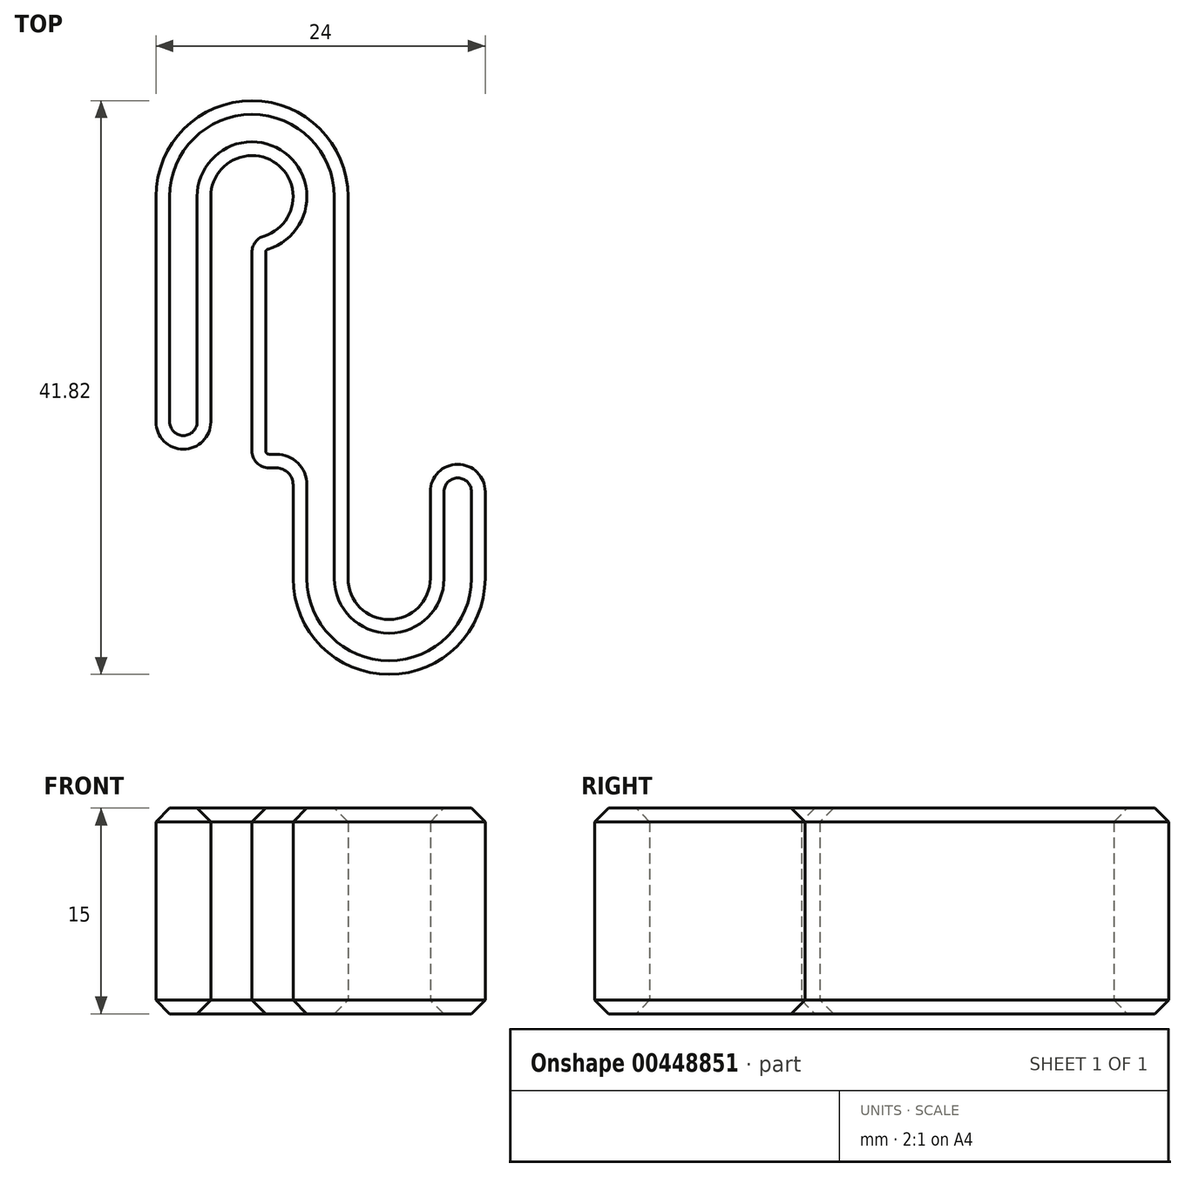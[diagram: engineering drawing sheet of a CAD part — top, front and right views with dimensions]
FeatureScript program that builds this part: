
annotation { "Feature Type Name" : "Feature", "Feature Type Description" : "" }
export const myFeature = defineFeature(function(context is Context, id is Id, definition is map)
    precondition{}
    {
        {
            var Q0;
            Q0=qCreatedBy(makeId("Top.planeOp"),FACE);
            var sketch = newSketch(context, id + "F0", { "sketchPlane" : qUnion([Q0])});
            skLineSegment(sketch, "E0.left", {"start": v(-10, 8.42) * mm, "end": v(-10, -8) * mm});
            skLineSegment(sketch, "E0.right", {"start": v(0, 8.42) * mm, "end": v(0, -19.4) * mm});
            skLineSegment(sketch, "E1.left", {"start": v(10, 13.42) * mm, "end": v(10, -13.09) * mm});
            skArc(sketch, "E2", {"start": v(0, 8.42) * mm, "mid": v(-5, 13.42) * mm, "end": v(-10, 8.42) * mm});
            skArc(sketch, "E3", {"start": v(0, -19.4) * mm, "mid": v(5, -24.4) * mm, "end": v(10, -19.4) * mm});
            skPoint(sketch, "E4.orphan", {"position": v(0, -24.4) * mm});
            skLineSegment(sketch, "E5", {"start": v(10, -13.09) * mm, "end": v(10, -19.4) * mm});
            skLineSegment(sketch, "E6", {"start": v(-10, -8) * mm, "end": v(-10, -24.4) * mm});
            skArc(sketch, "E7.0.startCap", {"start": v(-12, 8.42) * mm, "mid": v(-10, 10.42) * mm, "end": v(-8, 8.42) * mm});
            skArc(sketch, "E7.0.endCap", {"start": v(-8, -8) * mm, "mid": v(-10, -10) * mm, "end": v(-12, -8) * mm});
            skLineSegment(sketch, "E7.0.left", {"start": v(-8, 8.42) * mm, "end": v(-8, -8) * mm});
            skLineSegment(sketch, "E7.0.right", {"start": v(-12, 8.42) * mm, "end": v(-12, -8) * mm});
            skArc(sketch, "E7.1.startCap", {"start": v(2, 8.42) * mm, "mid": v(0, 6.42) * mm, "end": v(-2, 8.42) * mm});
            skArc(sketch, "E7.1.endCap", {"start": v(-8, 8.42) * mm, "mid": v(-10, 6.42) * mm, "end": v(-12, 8.42) * mm});
            skArc(sketch, "E7.1.left", {"start": v(-2, 8.42) * mm, "mid": v(-5, 11.42) * mm, "end": v(-8, 8.42) * mm});
            skArc(sketch, "E7.1.right", {"start": v(2, 8.42) * mm, "mid": v(-5, 15.42) * mm, "end": v(-12, 8.42) * mm});
            skArc(sketch, "E7.2.startCap", {"start": v(-2, 8.42) * mm, "mid": v(0, 10.42) * mm, "end": v(2, 8.42) * mm});
            skArc(sketch, "E7.2.endCap", {"start": v(2, -19.4) * mm, "mid": v(0, -21.4) * mm, "end": v(-2, -19.4) * mm});
            skLineSegment(sketch, "E7.2.left", {"start": v(2, 8.42) * mm, "end": v(2, -19.4) * mm});
            skLineSegment(sketch, "E7.2.right", {"start": v(-2, -12.58) * mm, "end": v(-2, -19.4) * mm});
            skArc(sketch, "E7.3.startCap", {"start": v(-2, -19.4) * mm, "mid": v(0, -17.4) * mm, "end": v(2, -19.4) * mm});
            skArc(sketch, "E7.3.endCap", {"start": v(8, -19.4) * mm, "mid": v(10, -17.4) * mm, "end": v(12, -19.4) * mm});
            skArc(sketch, "E7.3.left", {"start": v(2, -19.4) * mm, "mid": v(5, -22.4) * mm, "end": v(8, -19.4) * mm});
            skArc(sketch, "E7.3.right", {"start": v(-2, -19.4) * mm, "mid": v(5, -26.4) * mm, "end": v(12, -19.4) * mm});
            skArc(sketch, "E7.4.startCap", {"start": v(8, -13.09) * mm, "mid": v(10, -11.09) * mm, "end": v(12, -13.09) * mm});
            skArc(sketch, "E7.4.endCap", {"start": v(12, -19.4) * mm, "mid": v(10, -21.4) * mm, "end": v(8, -19.4) * mm});
            skLineSegment(sketch, "E7.4.left", {"start": v(12, -13.09) * mm, "end": v(12, -19.4) * mm});
            skLineSegment(sketch, "E7.4.right", {"start": v(8, -13.09) * mm, "end": v(8, -19.4) * mm});
            skArc(sketch, "E8", {"start": v(-4.13, 5.55) * mm, "mid": v(-3.21, 10.83) * mm, "end": v(-8, 8.42) * mm});
            skLineSegment(sketch, "E9", {"start": v(-5, 4.38) * mm, "end": v(-5, -10.12) * mm});
            skLineSegment(sketch, "E10", {"start": v(-3.77, -11.35) * mm, "end": v(-3.23, -11.35) * mm});
            skPoint(sketch, "E11.visualSharp", {"position": v(-5, -11.35) * mm});
            skArc(sketch, "E11.filletArc", {"start": v(-5, -10.12) * mm, "mid": v(-4.64, -10.99) * mm, "end": v(-3.77, -11.35) * mm});
            skArc(sketch, "E12.filletArc", {"start": v(-2, -12.58) * mm, "mid": v(-2.36, -11.7) * mm, "end": v(-3.23, -11.35) * mm});
            skPoint(sketch, "E13.visualSharp", {"position": v(-5, 5.42) * mm});
            skArc(sketch, "E13.filletArc", {"start": v(-4.13, 5.55) * mm, "mid": v(-4.76, 5.1) * mm, "end": v(-5, 4.38) * mm});
            skLineSegment(sketch, "E14", {"start": v(-2, 8.42) * mm, "end": v(-2, 1.47) * mm});
            skSolve(sketch);
        }
        {
            var Q0;
            {var subQ0=sQuery(id+"F0.wireOp",EDGE,"E7.0.left");Q0=makeQuery(id+"F0.imprint","IMPRINT",FACE,{"disambiguationData":[TD([[makeQuery(id+"F0.imprint","IMPRINT",EDGE,{"derivedFrom":subQ0}),-1.0]])]});}
            var Q1;
            {var subQ0=sQuery(id+"F0.wireOp",EDGE,"E7.0.right");Q1=makeQuery(id+"F0.imprint","IMPRINT",FACE,{"disambiguationData":[TD([[makeQuery(id+"F0.imprint","IMPRINT",EDGE,{"derivedFrom":subQ0}),1.0]])]});}
            var Q2;
            {var subQ0=sQuery(id+"F0.wireOp",EDGE,"E2");var subQ1=sQuery(id+"F0.wireOp",EDGE,"E0.left");var subQ2=makeQuery(id+"F0.imprint","INTERSECT",VERTEX,{"derivedFrom":[subQ1,subQ0]});Q2=makeQuery(id+"F0.imprint","IMPRINT",FACE,{"disambiguationData":[TD([[makeQuery(id+"F0.imprint","IMPRINT",EDGE,{"disambiguationData":[TD([[subQ2,-1.0]])],"derivedFrom":subQ1}),-1.0]])]});}
            var Q3;
            {var subQ0=sQuery(id+"F0.wireOp",EDGE,"E2");var subQ1=sQuery(id+"F0.wireOp",EDGE,"E0.left");var subQ2=makeQuery(id+"F0.imprint","INTERSECT",VERTEX,{"derivedFrom":[subQ1,subQ0]});Q3=makeQuery(id+"F0.imprint","IMPRINT",FACE,{"disambiguationData":[TD([[makeQuery(id+"F0.imprint","IMPRINT",EDGE,{"disambiguationData":[TD([[subQ2,-1.0]])],"derivedFrom":subQ1}),1.0]])]});}
            var Q4;
            {var subQ5=sQuery(id+"F0.wireOp",EDGE,"E7.1.left");Q4=makeQuery(id+"F0.imprint","IMPRINT",FACE,{"disambiguationData":[TD([[makeQuery(id+"F0.imprint","IMPRINT",EDGE,{"derivedFrom":subQ5}),-1.0]])]});}
            var Q5;
            {var subQ5=sQuery(id+"F0.wireOp",EDGE,"E7.1.right");Q5=makeQuery(id+"F0.imprint","IMPRINT",FACE,{"disambiguationData":[TD([[makeQuery(id+"F0.imprint","IMPRINT",EDGE,{"derivedFrom":subQ5}),1.0]])]});}
            var Q6;
            {var subQ0=sQuery(id+"F0.wireOp",EDGE,"E2");var subQ1=sQuery(id+"F0.wireOp",EDGE,"E0.right");var subQ2=makeQuery(id+"F0.imprint","INTERSECT",VERTEX,{"derivedFrom":[subQ1,subQ0]});Q6=makeQuery(id+"F0.imprint","IMPRINT",FACE,{"disambiguationData":[TD([[makeQuery(id+"F0.imprint","IMPRINT",EDGE,{"disambiguationData":[TD([[subQ2,-1.0]])],"derivedFrom":subQ1}),1.0]])]});}
            var Q7;
            {var subQ0=sQuery(id+"F0.wireOp",EDGE,"E2");var subQ1=sQuery(id+"F0.wireOp",EDGE,"E0.right");var subQ2=makeQuery(id+"F0.imprint","INTERSECT",VERTEX,{"derivedFrom":[subQ1,subQ0]});Q7=makeQuery(id+"F0.imprint","IMPRINT",FACE,{"disambiguationData":[TD([[makeQuery(id+"F0.imprint","IMPRINT",EDGE,{"disambiguationData":[TD([[subQ2,-1.0]])],"derivedFrom":subQ1}),-1.0]])]});}
            var Q8;
            {var subQ5=sQuery(id+"F0.wireOp",EDGE,"E7.2.right");Q8=makeQuery(id+"F0.imprint","IMPRINT",FACE,{"disambiguationData":[TD([[makeQuery(id+"F0.imprint","IMPRINT",EDGE,{"derivedFrom":subQ5}),1.0]])]});}
            var Q9;
            {var subQ5=sQuery(id+"F0.wireOp",EDGE,"E7.2.left");Q9=makeQuery(id+"F0.imprint","IMPRINT",FACE,{"disambiguationData":[TD([[makeQuery(id+"F0.imprint","IMPRINT",EDGE,{"derivedFrom":subQ5}),-1.0]])]});}
            var Q10;
            {var subQ0=sQuery(id+"F0.wireOp",EDGE,"E3");var subQ1=sQuery(id+"F0.wireOp",EDGE,"E0.right");var subQ2=makeQuery(id+"F0.imprint","INTERSECT",VERTEX,{"derivedFrom":[subQ1,subQ0]});Q10=makeQuery(id+"F0.imprint","IMPRINT",FACE,{"disambiguationData":[TD([[makeQuery(id+"F0.imprint","IMPRINT",EDGE,{"disambiguationData":[TD([[subQ2,1.0]])],"derivedFrom":subQ1}),1.0]])]});}
            var Q11;
            {var subQ0=sQuery(id+"F0.wireOp",EDGE,"E3");var subQ1=sQuery(id+"F0.wireOp",EDGE,"E0.right");var subQ2=makeQuery(id+"F0.imprint","INTERSECT",VERTEX,{"derivedFrom":[subQ1,subQ0]});Q11=makeQuery(id+"F0.imprint","IMPRINT",FACE,{"disambiguationData":[TD([[makeQuery(id+"F0.imprint","IMPRINT",EDGE,{"disambiguationData":[TD([[subQ2,1.0]])],"derivedFrom":subQ1}),-1.0]])]});}
            var Q12;
            {var subQ5=sQuery(id+"F0.wireOp",EDGE,"E7.3.right");Q12=makeQuery(id+"F0.imprint","IMPRINT",FACE,{"disambiguationData":[TD([[makeQuery(id+"F0.imprint","IMPRINT",EDGE,{"derivedFrom":subQ5}),1.0]])]});}
            var Q13;
            {var subQ5=sQuery(id+"F0.wireOp",EDGE,"E7.3.left");Q13=makeQuery(id+"F0.imprint","IMPRINT",FACE,{"disambiguationData":[TD([[makeQuery(id+"F0.imprint","IMPRINT",EDGE,{"derivedFrom":subQ5}),-1.0]])]});}
            var Q14;
            {var subQ0=sQuery(id+"F0.wireOp",EDGE,"E5");var subQ1=sQuery(id+"F0.wireOp",EDGE,"E3");var subQ2=makeQuery(id+"F0.imprint","INTERSECT",VERTEX,{"derivedFrom":[subQ1,subQ0]});Q14=makeQuery(id+"F0.imprint","IMPRINT",FACE,{"disambiguationData":[TD([[makeQuery(id+"F0.imprint","IMPRINT",EDGE,{"disambiguationData":[TD([[subQ2,1.0]])],"derivedFrom":subQ1}),1.0]])]});}
            var Q15;
            {var subQ0=sQuery(id+"F0.wireOp",EDGE,"E5");var subQ1=sQuery(id+"F0.wireOp",EDGE,"E3");var subQ2=makeQuery(id+"F0.imprint","INTERSECT",VERTEX,{"derivedFrom":[subQ1,subQ0]});Q15=makeQuery(id+"F0.imprint","IMPRINT",FACE,{"disambiguationData":[TD([[makeQuery(id+"F0.imprint","IMPRINT",EDGE,{"disambiguationData":[TD([[subQ2,1.0]])],"derivedFrom":subQ1}),-1.0]])]});}
            var Q16;
            {var subQ0=sQuery(id+"F0.wireOp",EDGE,"E7.4.left");Q16=makeQuery(id+"F0.imprint","IMPRINT",FACE,{"disambiguationData":[TD([[makeQuery(id+"F0.imprint","IMPRINT",EDGE,{"derivedFrom":subQ0}),-1.0]])]});}
            var Q17;
            {var subQ0=sQuery(id+"F0.wireOp",EDGE,"E7.4.right");Q17=makeQuery(id+"F0.imprint","IMPRINT",FACE,{"disambiguationData":[TD([[makeQuery(id+"F0.imprint","IMPRINT",EDGE,{"derivedFrom":subQ0}),1.0]])]});}
            var Q18;
            {var subQ0=sQuery(id+"F0.wireOp",EDGE,"E7.2.startCap");var subQ1=sQuery(id+"F0.wireOp",EDGE,"E2");var subQ2=makeQuery(id+"F0.imprint","INTERSECT",VERTEX,{"derivedFrom":[subQ1,subQ0]});Q18=makeQuery(id+"F0.imprint","IMPRINT",FACE,{"disambiguationData":[TD([[makeQuery(id+"F0.imprint","IMPRINT",EDGE,{"disambiguationData":[TD([[subQ2,-1.0]])],"derivedFrom":subQ1}),1.0]])]});}
            extrude(context, id + "F1", {"entities" : qUnion([Q0, Q1, Q2, Q3, Q4, Q5, Q6, Q7, Q8, Q9, Q10, Q11, Q12, Q13, Q14, Q15, Q16, Q17, Q18]), "depth" : 15 * mm});
        }
        {
            var Q0;
            Q0=makeQuery(id+"F1.opExtrude","CAP_FACE",FACE,{"disambiguationData":[OSD([sQuery(id+"F0.wireOp",EDGE,"E7.0.endCap"),sQuery(id+"F0.wireOp",EDGE,"E7.0.left"),sQuery(id+"F0.wireOp",EDGE,"E7.0.right"),sQuery(id+"F0.wireOp",EDGE,"E7.1.left"),sQuery(id+"F0.wireOp",EDGE,"E7.1.right"),sQuery(id+"F0.wireOp",EDGE,"E7.2.left"),sQuery(id+"F0.wireOp",EDGE,"E7.2.right"),sQuery(id+"F0.wireOp",EDGE,"E7.3.left"),sQuery(id+"F0.wireOp",EDGE,"E7.3.right"),sQuery(id+"F0.wireOp",EDGE,"E7.4.startCap"),sQuery(id+"F0.wireOp",EDGE,"E7.4.left"),sQuery(id+"F0.wireOp",EDGE,"E7.4.right")])],"isStart":false});
            var Q1;
            Q1=makeQuery(id+"F1.opExtrude","CAP_FACE",FACE,{"disambiguationData":[OSD([sQuery(id+"F0.wireOp",EDGE,"E7.0.endCap"),sQuery(id+"F0.wireOp",EDGE,"E7.0.left"),sQuery(id+"F0.wireOp",EDGE,"E7.0.right"),sQuery(id+"F0.wireOp",EDGE,"E7.1.left"),sQuery(id+"F0.wireOp",EDGE,"E7.1.right"),sQuery(id+"F0.wireOp",EDGE,"E7.2.left"),sQuery(id+"F0.wireOp",EDGE,"E7.2.right"),sQuery(id+"F0.wireOp",EDGE,"E7.3.left"),sQuery(id+"F0.wireOp",EDGE,"E7.3.right"),sQuery(id+"F0.wireOp",EDGE,"E7.4.startCap"),sQuery(id+"F0.wireOp",EDGE,"E7.4.left"),sQuery(id+"F0.wireOp",EDGE,"E7.4.right")])],"isStart":true});
            chamfer(context, id + "F2", {"entities" : qUnion([Q0, Q1]), "width" : 1 * mm, "tangentPropagation" : true});
        }
    });
